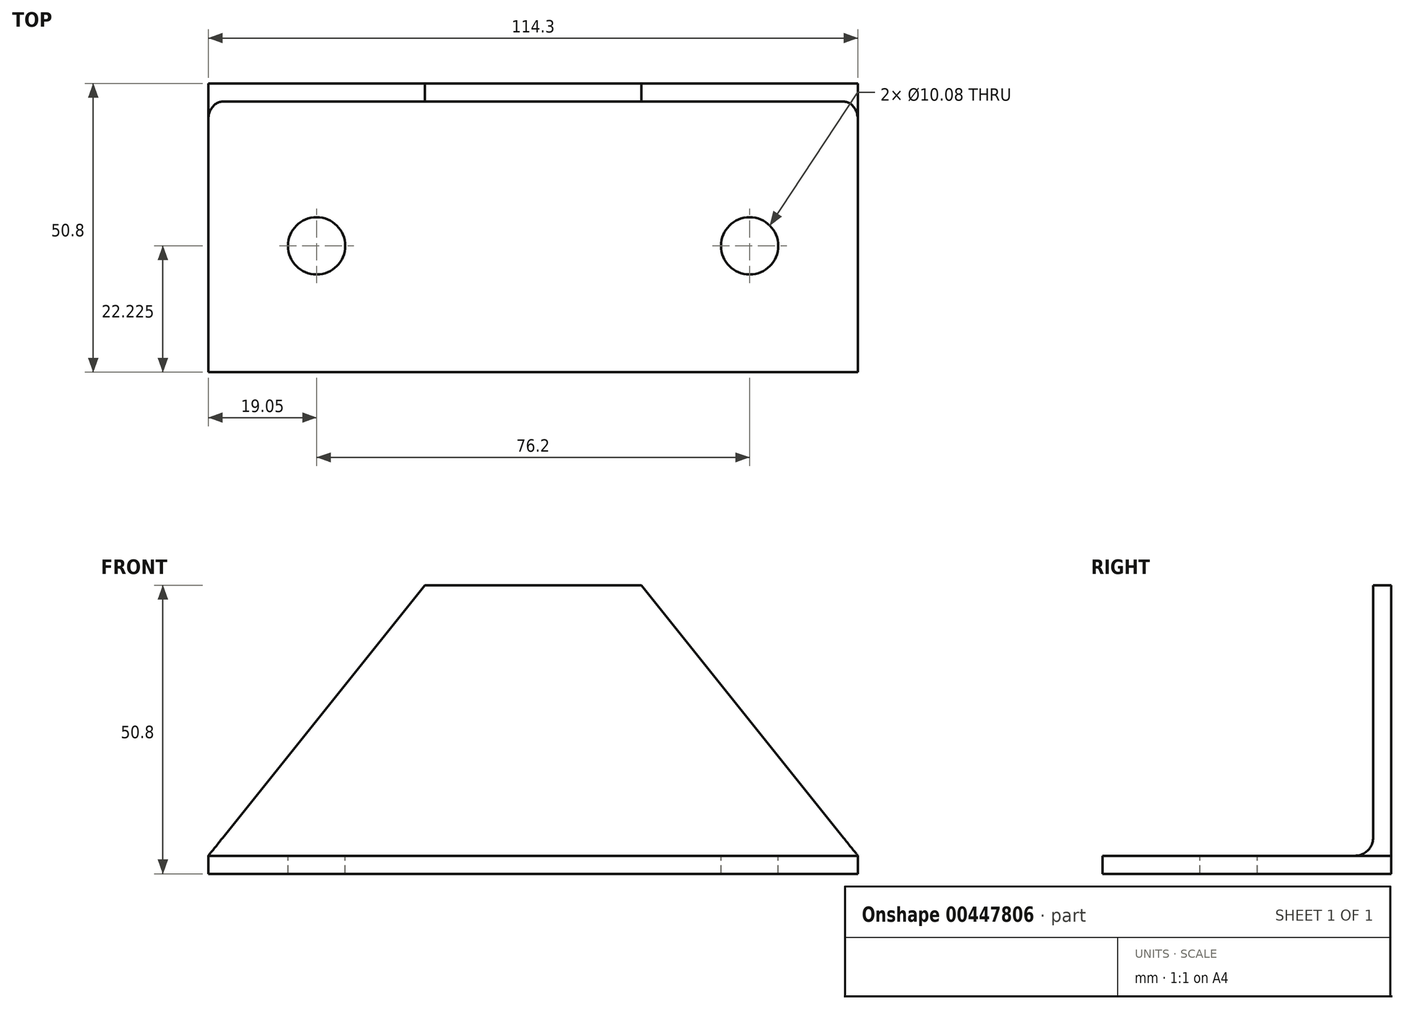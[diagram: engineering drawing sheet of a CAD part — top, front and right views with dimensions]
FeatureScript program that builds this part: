
annotation { "Feature Type Name" : "Feature", "Feature Type Description" : "" }
export const myFeature = defineFeature(function(context is Context, id is Id, definition is map)
    precondition{}
    {
        {
            var Q0;
            Q0=qCreatedBy(makeId("Right.planeOp"),FACE);
            var sketch = newSketch(context, id + "F0", { "sketchPlane" : qUnion([Q0])});
            skLineSegment(sketch, "E0", {"start": v(0, 0) * mm, "end": v(50.8, 0) * mm});
            skLineSegment(sketch, "E1", {"start": v(50.8, 0) * mm, "end": v(50.8, 50.8) * mm});
            skLineSegment(sketch, "E2", {"start": v(50.8, 50.8) * mm, "end": v(47.62, 50.8) * mm});
            skLineSegment(sketch, "E3", {"start": v(47.62, 50.8) * mm, "end": v(47.62, 6.35) * mm});
            skLineSegment(sketch, "E4", {"start": v(44.45, 3.17) * mm, "end": v(0, 3.17) * mm});
            skLineSegment(sketch, "E5", {"start": v(0, 3.17) * mm, "end": v(0, 0) * mm});
            skPoint(sketch, "E6.visualSharp", {"position": v(47.62, 3.17) * mm});
            skArc(sketch, "E6.filletArc", {"start": v(44.45, 3.17) * mm, "mid": v(46.7, 4.1) * mm, "end": v(47.62, 6.35) * mm});
            skSolve(sketch);
        }
        {
            var Q0;
            Q0 = qSketchRegion(id + "F0", true);
            extrude(context, id + "F1", {"entities" : qUnion([Q0]), "depth" : 152.4 * mm});
        }
        {
            var Q0;
            Q0=makeQuery(id+"F1.opExtrude","SWEPT_FACE",FACE,{"disambiguationData":[OSD([sQuery(id+"F0.wireOp",EDGE,"E1")])]});
            var sketch = newSketch(context, id + "F2", { "sketchPlane" : qUnion([Q0])});
            skLineSegment(sketch, "E7", {"start": v(-76.2, 50.8) * mm, "end": v(-57.15, 50.8) * mm});
            skLineSegment(sketch, "E8", {"start": v(-57.15, 50.8) * mm, "end": v(-95.25, 50.8) * mm});
            skLineSegment(sketch, "E9", {"start": v(-133.35, 3.17) * mm, "end": v(-95.25, 50.8) * mm});
            skLineSegment(sketch, "E10", {"start": v(-76.2, 50.8) * mm, "end": v(-76.2, 8.12) * mm});
            skLineSegment(sketch, "E11.MirrorCS", {"start": v(-19.05, 3.17) * mm, "end": v(-57.15, 50.8) * mm});
            skLineSegment(sketch, "E12", {"start": v(-19.05, 3.17) * mm, "end": v(-19.05, 0) * mm});
            skLineSegment(sketch, "E13", {"start": v(-19.05, 0) * mm, "end": v(0, 0) * mm});
            skLineSegment(sketch, "E14", {"start": v(0, 0) * mm, "end": v(0, 50.8) * mm});
            skLineSegment(sketch, "E15", {"start": v(0, 50.8) * mm, "end": v(-57.15, 50.8) * mm});
            skLineSegment(sketch, "E16", {"start": v(-95.25, 50.8) * mm, "end": v(-152.4, 50.8) * mm});
            skLineSegment(sketch, "E17", {"start": v(-152.4, 50.8) * mm, "end": v(-152.4, 0) * mm});
            skLineSegment(sketch, "E18", {"start": v(-152.4, 0) * mm, "end": v(-133.35, 0) * mm});
            skLineSegment(sketch, "E19", {"start": v(-133.35, 0) * mm, "end": v(-133.35, 3.17) * mm});
            skPoint(sketch, "E20.end.orphan", {"position": v(-95.25, 0) * mm});
            skSolve(sketch);
        }
        {
            var Q0;
            Q0 = qSketchRegion(id + "F2", true);
            extrude(context, id + "F3", {"entities" : qUnion([Q0]), "operationType" : NewBodyOperationType.REMOVE, "endBound" : BoundingType.THROUGH_ALL, "oppositeDirection" : true, "depth" : 25.4 * mm});
        }
        {
            var Q0;
            Q0=makeQuery(id+"F1.opExtrude","SWEPT_FACE",FACE,{"disambiguationData":[OSD([sQuery(id+"F0.wireOp",EDGE,"E4")])]});
            var sketch = newSketch(context, id + "F4", { "sketchPlane" : qUnion([Q0])});
            skLineSegment(sketch, "E21", {"start": v(19.05, 22.22) * mm, "end": v(57.15, 22.22) * mm});
            skCircle(sketch, "E22", {"center": v(38.1, 22.22) * mm, "radius": 5.04 * mm});
            skLineSegment(sketch, "E23", {"start": v(76.2, 0) * mm, "end": v(76.2, 28.3) * mm});
            skCircle(sketch, "E24.MirrorC", {"center": v(114.3, 22.22) * mm, "radius": 5.04 * mm});
            skLineSegment(sketch, "E25.MirrorCS", {"start": v(133.35, 22.22) * mm, "end": v(95.25, 22.22) * mm});
            skSolve(sketch);
        }
        {
            var Q0;
            Q0 = qSketchRegion(id + "F4", true);
            extrude(context, id + "F5", {"entities" : qUnion([Q0]), "operationType" : NewBodyOperationType.REMOVE, "oppositeDirection" : true, "depth" : 25.4 * mm});
        }
    });
